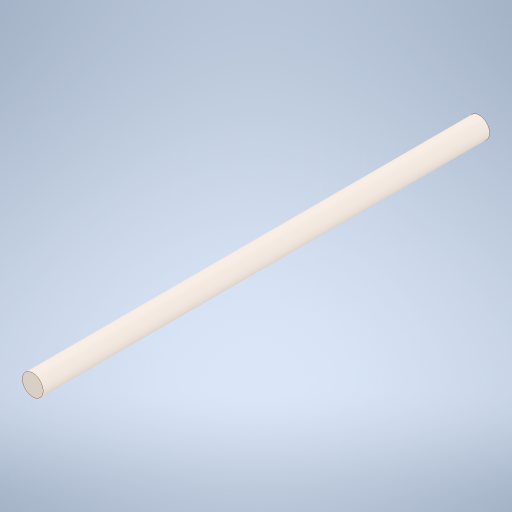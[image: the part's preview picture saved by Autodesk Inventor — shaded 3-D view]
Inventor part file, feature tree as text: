
AUTODESK INVENTOR PART (.ipt)
format: ipt  version: 2024 (Build 280153000, 153)  size: 242,176 bytes
history: native  units: mm
features: extrude x1, sketch x1, projected_geometry x1, other x1
ambient origin geometry x8: Origin, YZ Plane, XZ Plane, XY Plane, X Axis, Y Axis, Z Axis, Center Point
bodies: Solid1 (feature_tree)
feature tree (4):
  extrude  "Extrusion2"  [1 undecoded]
  sketch  "Sketch2"  dims[d2=30.0mm d3=0.0mm]
  projected_geometry  "Projected Loop2"
  other  "Boss-Extrude1"
note: 1 required parameter value undecoded (feature->parameter linkage not recoverable at this tier; creation-order binding heuristic only, values carry confidence <= 0.55)
